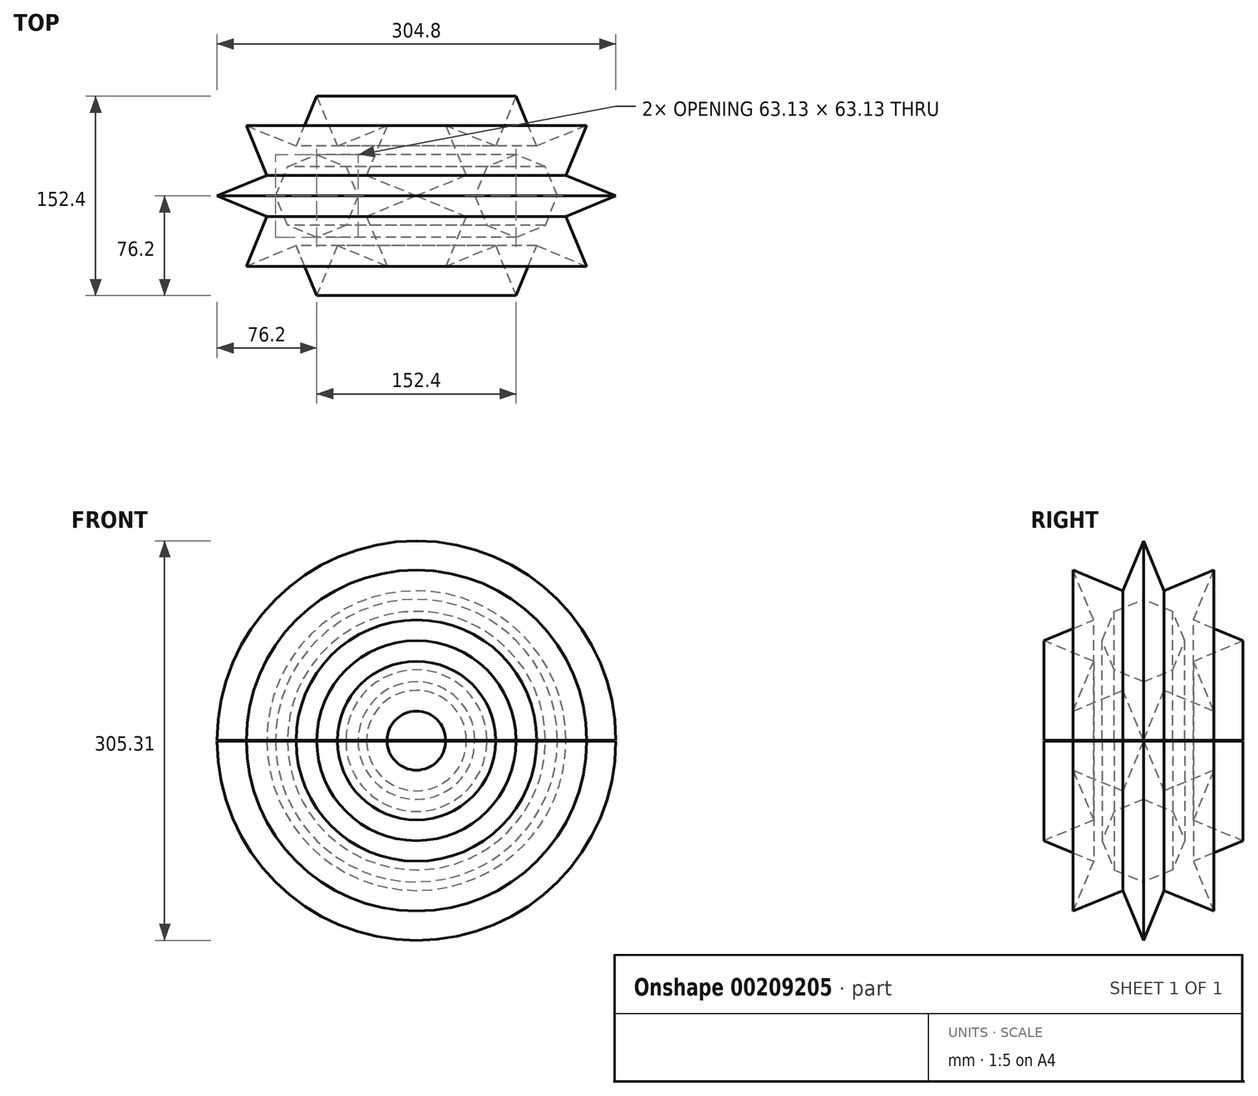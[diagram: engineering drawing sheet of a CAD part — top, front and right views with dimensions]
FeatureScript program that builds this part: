
annotation { "Feature Type Name" : "Feature", "Feature Type Description" : "" }
export const myFeature = defineFeature(function(context is Context, id is Id, definition is map)
    precondition{}
    {
        {
            var Q0;
            Q0=qCreatedBy(makeId("Top.planeOp"),FACE);
            var sketch = newSketch(context, id + "F0", { "sketchPlane" : qUnion([Q0])});
            skLineSegment(sketch, "E0", {"start": v(0, 76.2) * mm, "end": v(-53.88, -53.88) * mm});
            skLineSegment(sketch, "E1", {"start": v(-53.88, -53.88) * mm, "end": v(76.2, 0) * mm});
            skLineSegment(sketch, "E2", {"start": v(76.2, 0) * mm, "end": v(-53.88, 53.88) * mm});
            skLineSegment(sketch, "E3", {"start": v(-53.88, 53.88) * mm, "end": v(0, -76.2) * mm});
            skLineSegment(sketch, "E4", {"start": v(0, -76.2) * mm, "end": v(53.88, 53.88) * mm});
            skLineSegment(sketch, "E5", {"start": v(53.88, 53.88) * mm, "end": v(-76.2, 0) * mm});
            skLineSegment(sketch, "E6", {"start": v(-76.2, 0) * mm, "end": v(53.88, -53.88) * mm});
            skLineSegment(sketch, "E7", {"start": v(53.88, -53.88) * mm, "end": v(0, 76.2) * mm});
            skSolve(sketch);
        }
        {
            var Q0;
            Q0=qCreatedBy(makeId("Front.planeOp"),FACE);
            var sketch = newSketch(context, id + "F1", { "sketchPlane" : qUnion([Q0])});
            skArc(sketch, "E8", {"start": v(0, 0) * mm, "mid": v(-76.2, 76.2) * mm, "end": v(-152.4, 0) * mm});
            skSolve(sketch);
        }
        {
            var Q0;
            Q0 = qSketchRegion(id + "F0", true);
            var Q1;
            Q1=sQuery(id+"F1.wireOp",EDGE,"E8");
            sweep(context, id + "F2", {"profiles" : qUnion([Q0]), "path" : qUnion([Q1])});
        }
        {
            var Q0;
            Q0=qCreatedBy(makeId("Top.planeOp"),FACE);
            cPlane(context, id + "F3", {"entities" : qUnion([Q0]), "cplaneType" : CPlaneType.OFFSET, "offset" : 0.25 * mm, "oppositeDirection" : true, "width" : 152.4 * mm, "height" : 152.4 * mm});
        }
        {
            var Q0;
            Q0=makeQuery(id+"F2.opSweep","SWEPT_BODY",BODY,{"disambiguationData":[OSD([sQuery(id+"F0.wireOp",EDGE,"E0"),sQuery(id+"F0.wireOp",EDGE,"E1"),sQuery(id+"F0.wireOp",EDGE,"E2"),sQuery(id+"F0.wireOp",EDGE,"E3"),sQuery(id+"F0.wireOp",EDGE,"E4"),sQuery(id+"F0.wireOp",EDGE,"E5"),sQuery(id+"F0.wireOp",EDGE,"E6"),sQuery(id+"F0.wireOp",EDGE,"E7"),sQuery(id+"F1.wireOp",EDGE,"E8")])]});
            var Q1;
            Q1=qCreatedBy(id+"F3.planeOp",FACE);
            mirror(context, id + "F4", {"entities" : qUnion([Q0]), "mirrorPlane" : qUnion([Q1])});
        }
    });
